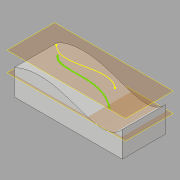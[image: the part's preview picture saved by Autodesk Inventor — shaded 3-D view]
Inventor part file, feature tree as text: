
AUTODESK INVENTOR PART (.ipt)
format: ipt  version: 2017.2 (Build 212233000, 233)  size: 103,424 bytes
history: native  units: mm
features: sketch x4, extrude x1, plane x1
ambient origin geometry x8: Origin, YZ Plane, XZ Plane, XY Plane, X Axis, Y Axis, Z Axis, Center Point
bodies: Solid1 (feature_tree)
feature tree (6):
  extrude  "Extrusion1"  Depth=4.5mm
  plane  "Work Plane1"
  sketch  "Sketch2"
  sketch  "3D Sketch1"
  sketch  "3D Sketch5"
  sketch  "Sketch1"  dims[d0=10.0mm d1=0.0mm d2=4.5mm]
